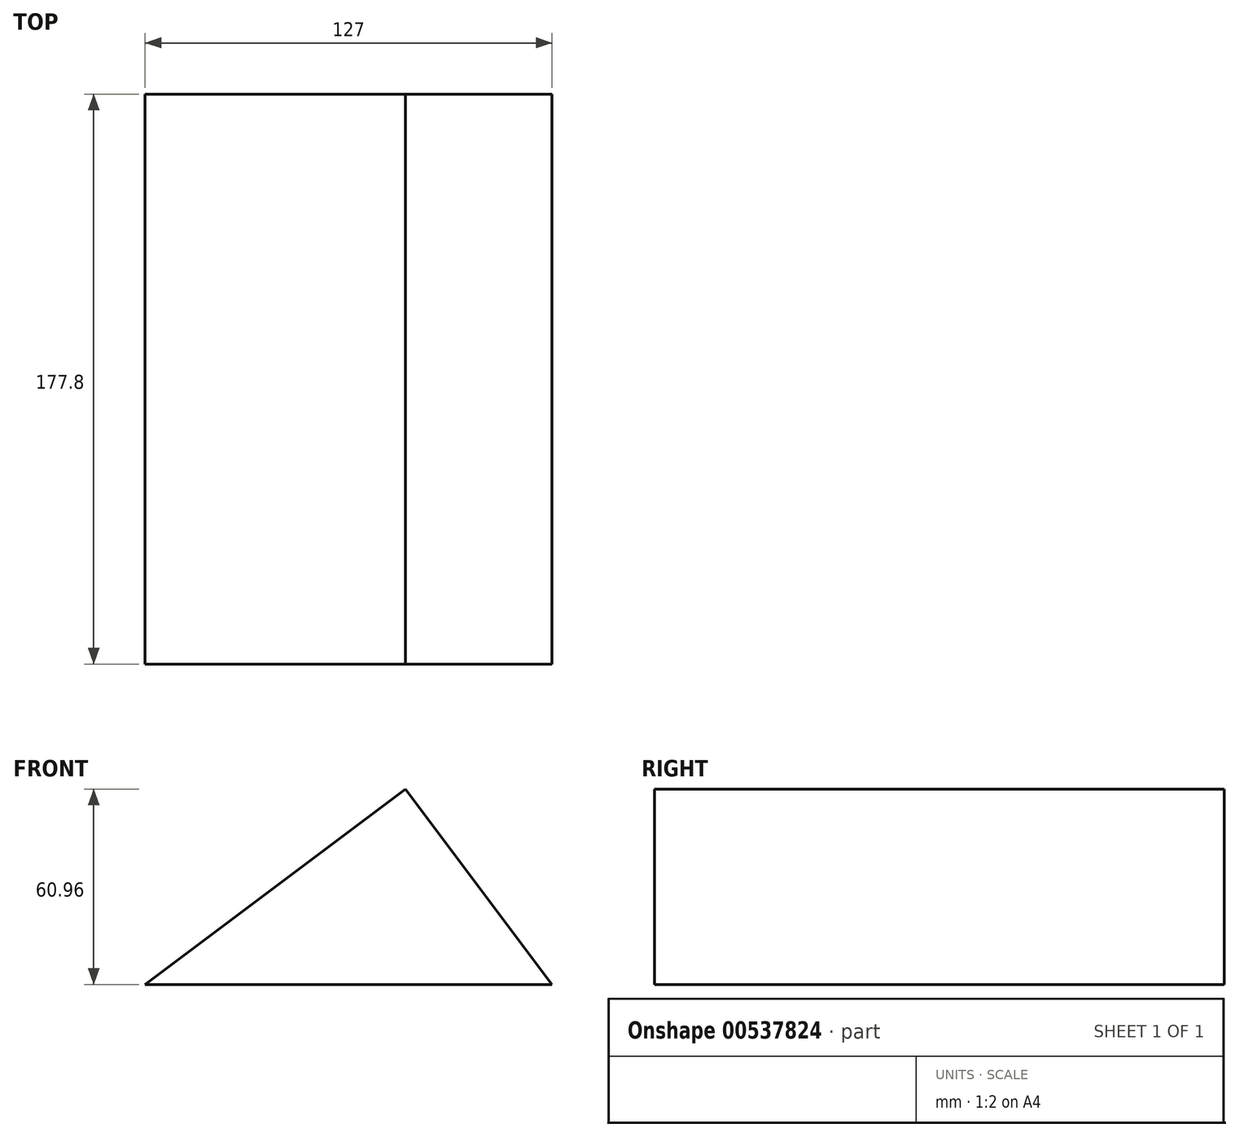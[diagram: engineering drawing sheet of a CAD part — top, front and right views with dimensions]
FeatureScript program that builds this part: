
annotation { "Feature Type Name" : "Feature", "Feature Type Description" : "" }
export const myFeature = defineFeature(function(context is Context, id is Id, definition is map)
    precondition{}
    {
        {
            var Q0;
            Q0=qCreatedBy(makeId("Front.planeOp"),FACE);
            var sketch = newSketch(context, id + "F0", { "sketchPlane" : qUnion([Q0])});
            skLineSegment(sketch, "E0", {"start": v(0, 60.96) * mm, "end": v(-81.28, 0) * mm});
            skLineSegment(sketch, "E1", {"start": v(0, 60.96) * mm, "end": v(45.72, 0) * mm});
            skLineSegment(sketch, "E2", {"start": v(45.72, 0) * mm, "end": v(-81.28, 0) * mm});
            skSolve(sketch);
        }
        {
            var Q0;
            Q0 = qSketchRegion(id + "F0", true);
            extrude(context, id + "F1", {"entities" : qUnion([Q0]), "depth" : 177.8 * mm, "offsetDistance" : 25.4 * mm});
        }
    });
